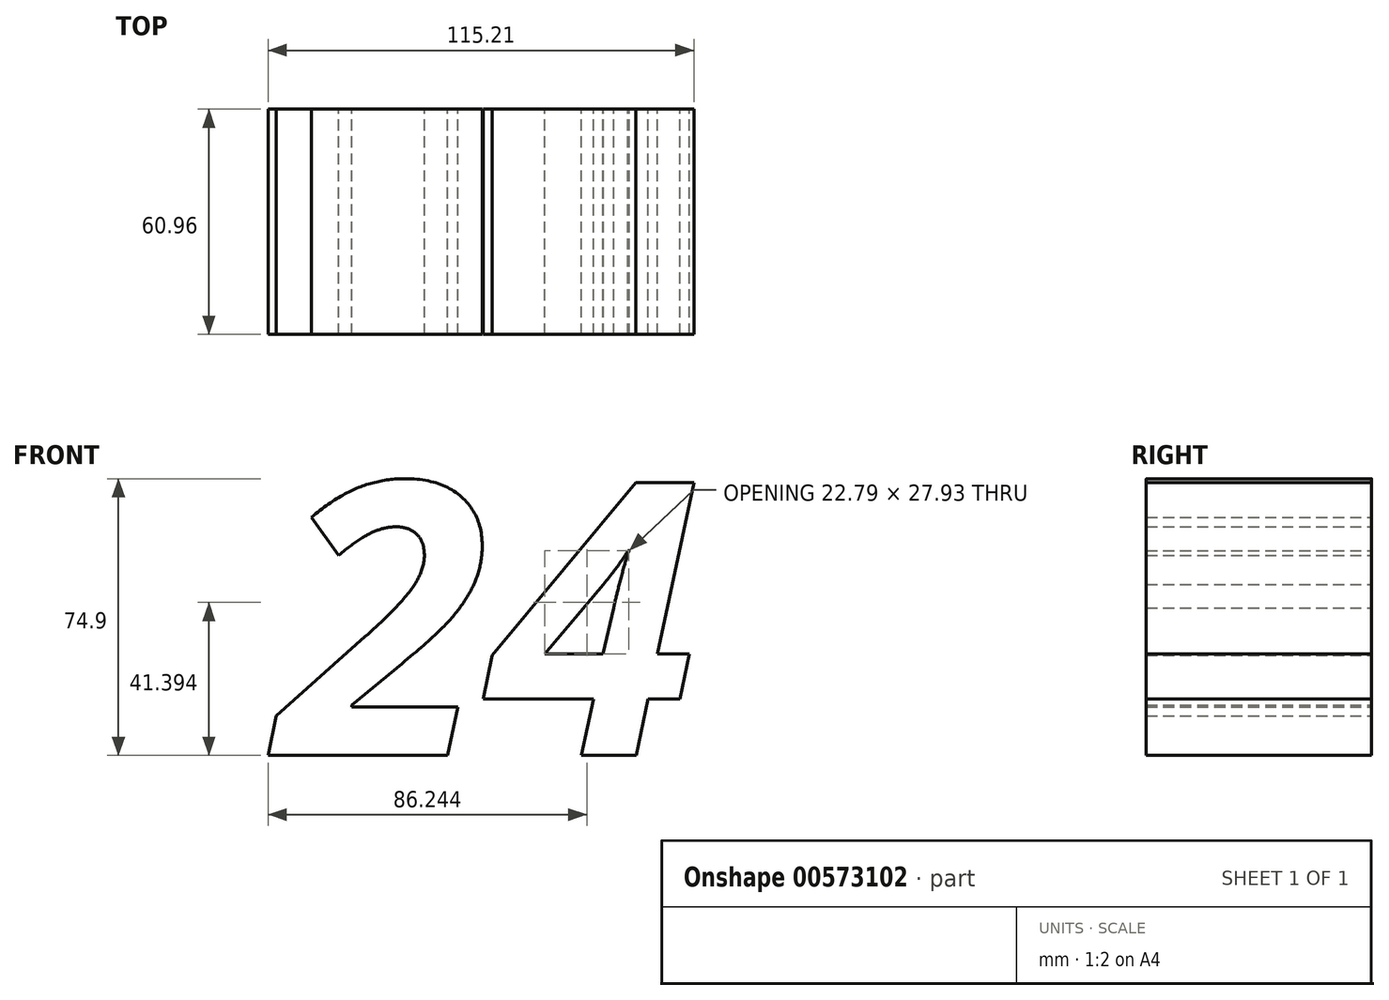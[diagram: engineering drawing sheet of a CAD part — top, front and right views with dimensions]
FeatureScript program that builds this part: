
annotation { "Feature Type Name" : "Feature", "Feature Type Description" : "" }
export const myFeature = defineFeature(function(context is Context, id is Id, definition is map)
    precondition{}
    {
        {
            var Q0;
            Q0=qCreatedBy(makeId("Front.planeOp"),FACE);
            var sketch = newSketch(context, id + "F0", { "sketchPlane" : qUnion([Q0])});
            skText(sketch, "E0", { "text": "24", "fontName": "OpenSans-BoldItalic.ttf"});
            const initialGuessF0  = {"E0": [-0.02933, -0.04127, 1, 0, 0.07448]};
            skSetInitialGuess(sketch, initialGuessF0);
            skSolve(sketch);
        }
        {
            var Q0;
            Q0 = qSketchRegion(id + "F0", true);
            extrude(context, id + "F1", {"entities" : qUnion([Q0]), "depth" : 60.96 * mm, "offsetDistance" : 25.4 * mm});
        }
    });
